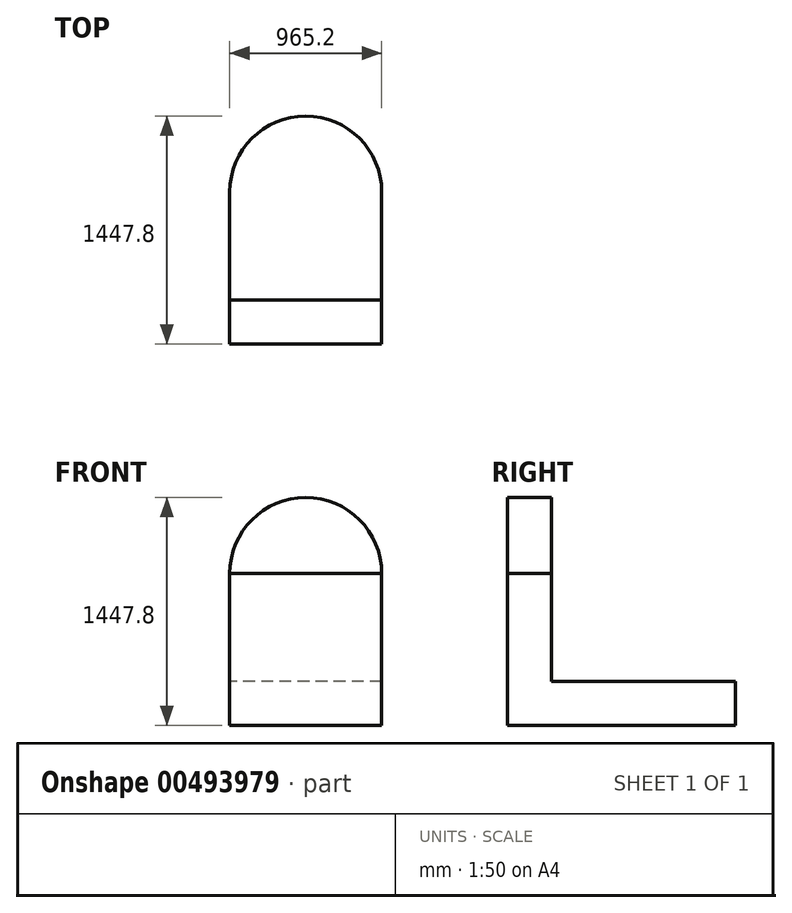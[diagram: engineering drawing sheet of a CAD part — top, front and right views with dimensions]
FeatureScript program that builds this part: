
annotation { "Feature Type Name" : "Feature", "Feature Type Description" : "" }
export const myFeature = defineFeature(function(context is Context, id is Id, definition is map)
    precondition{}
    {
        {
            var Q0;
            Q0=qCreatedBy(makeId("Right.planeOp"),FACE);
            var sketch = newSketch(context, id + "F0", { "sketchPlane" : qUnion([Q0])});
            skLineSegment(sketch, "E0", {"start": v(-279.4, 685.8) * mm, "end": v(0, 685.8) * mm});
            skLineSegment(sketch, "E1", {"start": v(0, 685.8) * mm, "end": v(0, 0) * mm});
            skLineSegment(sketch, "E2", {"start": v(0, 0) * mm, "end": v(685.8, 0) * mm});
            skLineSegment(sketch, "E3", {"start": v(685.8, 0) * mm, "end": v(685.8, -279.4) * mm});
            skLineSegment(sketch, "E4", {"start": v(685.8, -279.4) * mm, "end": v(-279.4, -279.4) * mm});
            skLineSegment(sketch, "E5", {"start": v(-279.4, -279.4) * mm, "end": v(-279.4, 685.8) * mm});
            skSolve(sketch);
        }
        {
            var Q0;
            Q0 = qSketchRegion(id + "F0", true);
            extrude(context, id + "F1", {"entities" : qUnion([Q0]), "endBound" : BoundingType.SYMMETRIC, "depth" : 965.2 * mm});
        }
        {
            var Q0;
            Q0=makeQuery(id+"F1.opExtrude","SWEPT_FACE",FACE,{"disambiguationData":[OSD([sQuery(id+"F0.wireOp",EDGE,"E1")])]});
            var sketch = newSketch(context, id + "F2", { "sketchPlane" : qUnion([Q0])});
            skArc(sketch, "E6", {"start": v(482.6, 685.8) * mm, "mid": v(0, 1168.4) * mm, "end": v(-482.6, 685.8) * mm});
            skLineSegment(sketch, "E7", {"start": v(-482.6, 685.8) * mm, "end": v(482.6, 685.8) * mm});
            skSolve(sketch);
        }
        {
            var Q0;
            Q0=makeQuery(id+"F1.opExtrude","SWEPT_FACE",FACE,{"disambiguationData":[OSD([sQuery(id+"F0.wireOp",EDGE,"E2")])]});
            var sketch = newSketch(context, id + "F3", { "sketchPlane" : qUnion([Q0])});
            skArc(sketch, "E8", {"start": v(482.6, 685.8) * mm, "mid": v(0, 1168.4) * mm, "end": v(-482.6, 685.8) * mm});
            skLineSegment(sketch, "E9", {"start": v(482.6, 685.8) * mm, "end": v(-482.6, 685.8) * mm});
            skSolve(sketch);
        }
        {
            var Q0;
            Q0 = qSketchRegion(id + "F3", true);
            extrude(context, id + "F4", {"entities" : qUnion([Q0]), "operationType" : NewBodyOperationType.ADD, "oppositeDirection" : true, "depth" : 279.4 * mm});
        }
        {
            var Q0;
            Q0 = qSketchRegion(id + "F2", true);
            extrude(context, id + "F5", {"entities" : qUnion([Q0]), "oppositeDirection" : true, "depth" : 279.4 * mm});
        }
    });
